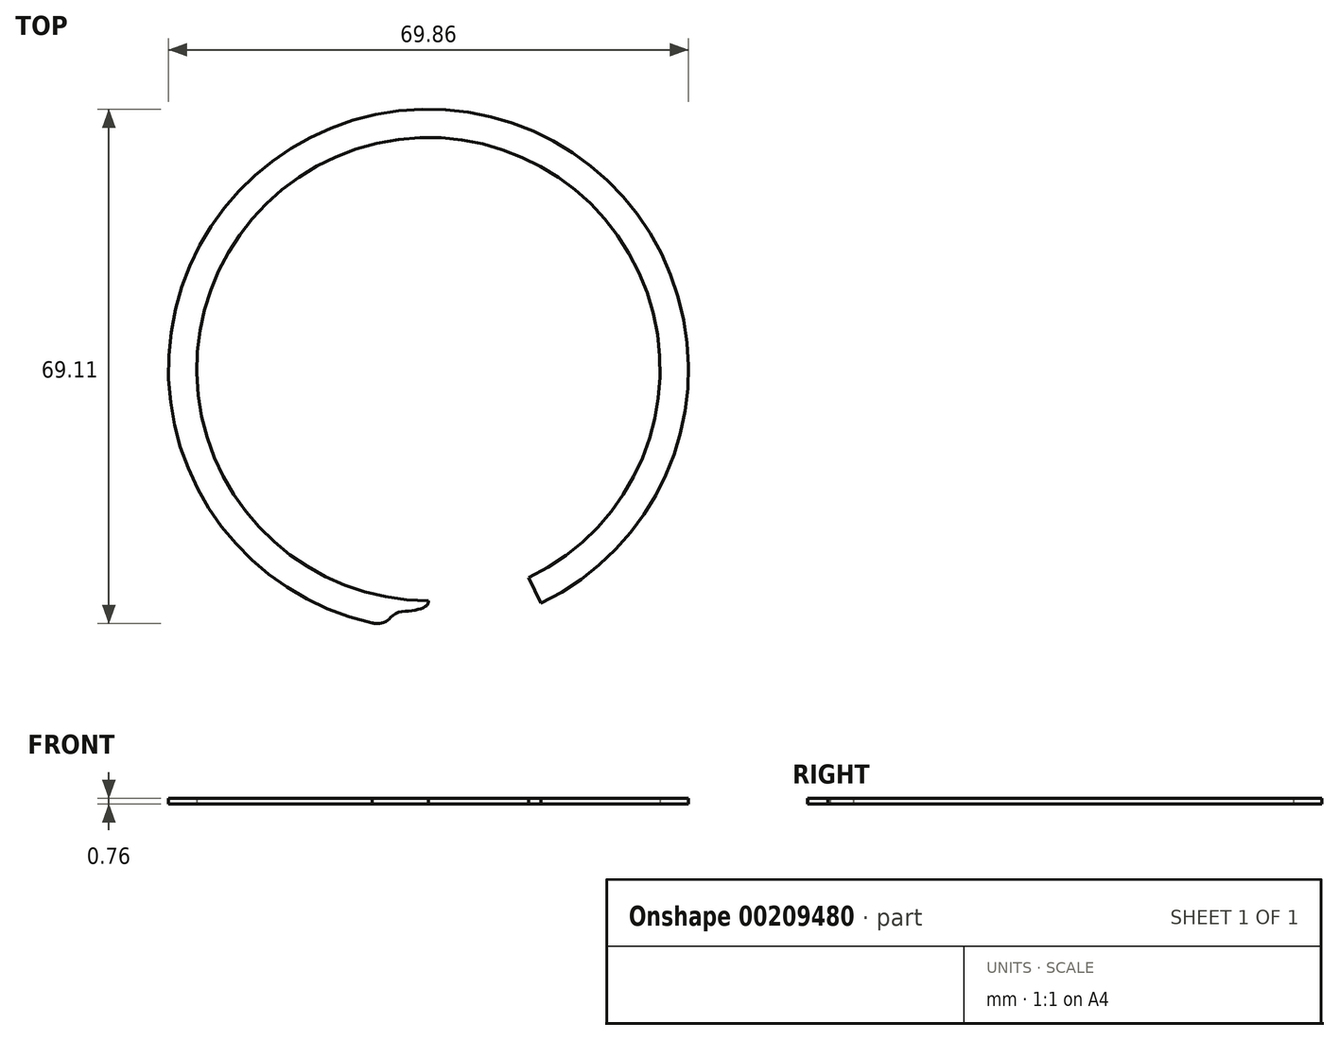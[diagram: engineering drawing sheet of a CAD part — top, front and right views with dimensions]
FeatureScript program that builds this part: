
annotation { "Feature Type Name" : "Feature", "Feature Type Description" : "" }
export const myFeature = defineFeature(function(context is Context, id is Id, definition is map)
    precondition{}
    {
        {
            var Q0;
            Q0=qCreatedBy(makeId("Top.planeOp"),FACE);
            var sketch = newSketch(context, id + "F0", { "sketchPlane" : qUnion([Q0])});
            skArc(sketch, "E0", {"start": v(15.13, -31.48) * mm, "mid": v(-4.14, 34.68) * mm, "end": v(-7.3, -34.15) * mm});
            skArc(sketch, "E1", {"start": v(13.48, -28.04) * mm, "mid": v(-6.91, 30.34) * mm, "end": v(0, -31.12) * mm});
            skLineSegment(sketch, "E2", {"start": v(13.48, -28.04) * mm, "end": v(15.13, -31.48) * mm});
            skLineSegment(sketch, "E3", {"start": v(0, -31.12) * mm, "end": v(0, -31.28) * mm});
            skFitSpline(sketch, "E4", {"points": [v(0, -31.12) * mm, v(-0.08, -31.56) * mm, v(-0.52, -31.97) * mm, v(-1.35, -32.27) * mm, v(-2.68, -32.53) * mm, v(-4.09, -32.7) * mm, v(-5.16, -33.43) * mm, v(-5.56, -33.8) * mm, v(-6.2, -34.1) * mm, v(-6.77, -34.18) * mm, v(-7.57, -34.1) * mm, v(-7.67, -34.1) * mm], "startDerivative": vector(0.4, -6.81) * mm, "endDerivative": vector(-8.76, -3.58) * mm});
            skSolve(sketch);
        }
        {
            var Q0;
            Q0 = qSketchRegion(id + "F0", true);
            extrude(context, id + "F1", {"entities" : qUnion([Q0]), "depth" : 0.76 * mm});
        }
    });
